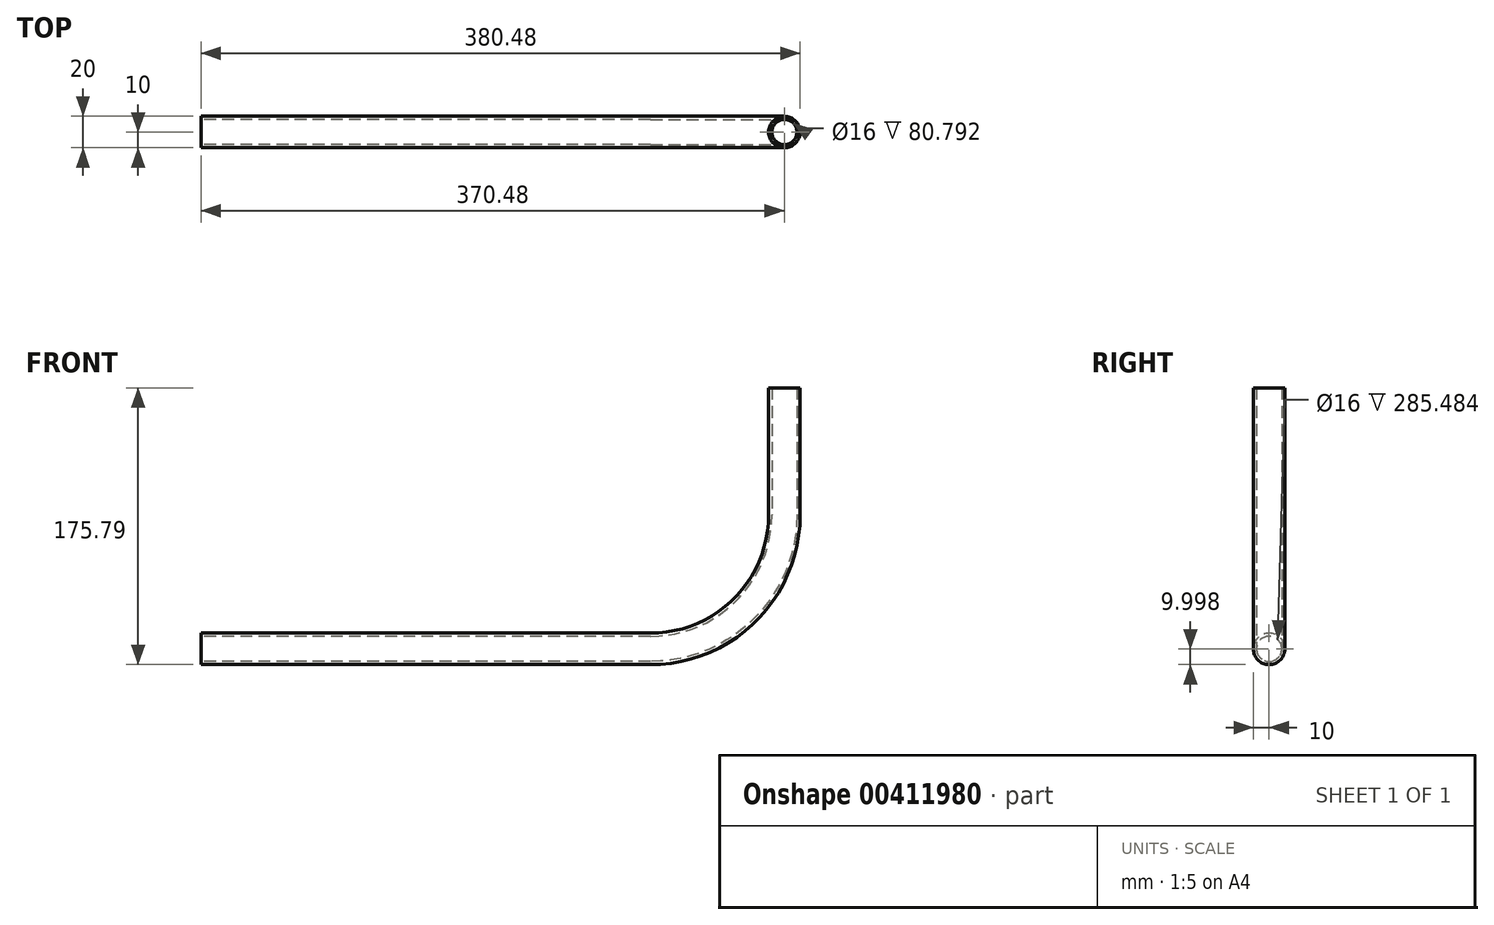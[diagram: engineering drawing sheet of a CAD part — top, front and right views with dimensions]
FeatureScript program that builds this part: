
annotation { "Feature Type Name" : "Feature", "Feature Type Description" : "" }
export const myFeature = defineFeature(function(context is Context, id is Id, definition is map)
    precondition{}
    {
        {
            var Q0;
            Q0=qCreatedBy(makeId("Top.planeOp"),FACE);
            var sketch = newSketch(context, id + "F0", { "sketchPlane" : qUnion([Q0])});
            skCircle(sketch, "E0", {"center": v(0, 0) * mm, "radius": 10 * mm});
            skCircle(sketch, "E1.0", {"center": v(0, 0) * mm, "radius": 8 * mm});
            skSolve(sketch);
        }
        {
            var Q0;
            Q0=qCreatedBy(makeId("Front.planeOp"),FACE);
            var sketch = newSketch(context, id + "F1", { "sketchPlane" : qUnion([Q0])});
            skLineSegment(sketch, "E2", {"start": v(0, 0) * mm, "end": v(0, -80.8) * mm});
            skLineSegment(sketch, "E3", {"start": v(-85, -165.8) * mm, "end": v(-370.48, -165.8) * mm});
            skPoint(sketch, "E4.visualSharp", {"position": v(0, -165.8) * mm});
            skArc(sketch, "E4.filletArc", {"start": v(-85, -165.8) * mm, "mid": v(-24.9, -140.9) * mm, "end": v(0, -80.8) * mm});
            skSolve(sketch);
        }
        {
            var Q0;
            Q0=makeQuery(id+"F0.imprint","IMPRINT",FACE,{"disambiguationData":[TD([[makeQuery(id+"F0.imprint","IMPRINT",EDGE,{"derivedFrom":sQuery(id+"F0.wireOp",EDGE,"E0")}),1.0]])]});
            var Q1;
            Q1=sQuery(id+"F1.wireOp",EDGE,"E4.filletArc");
            var Q2;
            Q2=sQuery(id+"F1.wireOp",EDGE,"E2");
            var Q3;
            Q3=sQuery(id+"F1.wireOp",EDGE,"E3");
            sweep(context, id + "F2", {"profiles" : qUnion([Q0]), "path" : qUnion([Q1, Q2, Q3])});
        }
    });
